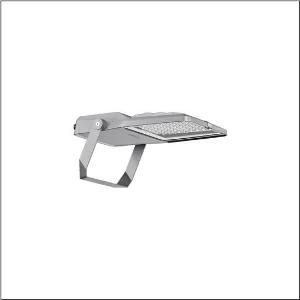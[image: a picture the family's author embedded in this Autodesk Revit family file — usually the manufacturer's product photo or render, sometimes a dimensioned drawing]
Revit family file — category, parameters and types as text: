
# Revit family: floodlight_fl_21_iq_mini___pl61_5xa7772c4c1a_7179
name_source: partatom
category: Lighting Fixtures
units: mm (PartAtom-declared; Revit-internal decimal feet)

## family parameters
Cut with Voids When Loaded = No
Host = Face
Light Source = No
Part Type = Normal
Room Calculation Point = No
Round Connector Dimension = Use Diameter
Shared = No

## types (1)
- --- (1 x LED, 12490 lm, 87.2 W, 4000K)
    Apparent Load = 87 VA
    CIE Flux Codes = 33 65 98 100 100
    Color Rendering = 70
    Color Temperature = 4000K
    Default Elevation = 1800 mm
    Description = Floodlight FL 21 iQ mini, floodlight, primary light control with lens, of PMMA, primary optical cover: protective disc, of toughened safety glass, transparent, light distribution: PL61, light emission: direct distribution, installation type: surface-mounted, LED, High Power LED, rated luminous flux: 12.490lm, luminous efficacy: 143lm/W, light colour: 740, colour temperature: 4000K, control: Street-Remote, Auto-Match, Temp-Guard, Night-Set, Smart-Wire, Desk-Remote (wireless, voltage-free reading and setting of iQ features in the workshop via application-optimized NFC function/RFID function), optimised constant luminous flux control (CLO 2.0), with terminal, 6-pole, mains connection: 220..240V, AC, 50/60Hz, start of lifetime: 87W, end of service life: 92W, reduction: 40W, luminaire housing, of diecast aluminium, powder-coated, Siteco® metallic grey (DB 702S), corrosivity category C5 mid according to DIN EN ISO 12944, sealing non-destructively replaceable, mounting bracket, of steel, galvanised, powder-coated, Siteco® metallic grey (DB 702S), protection rating (complete): IP66, insulation class (complete): insulation class II (safety insulation), certification: CE, ENEC, VDE, protection symbol: D, impact resistance: IK08, permissible operating ambient temperature: -40..+40°C, permissible operating ambient temperature for outdoor applications: -40..+50°C, standard: DIN EN 12944, LABS conformity tested according to VDMA 24364:2018-05, packaging unit: 1 piece

Light Distribution: PL61
    Height = 70 mm
    Lamp = 1 x LED
    Lamp Light Flux = 12490 lm
    Lamp Power = 87.2 W
    Lamp count = 1
    Length = 485 mm
    Luminous efficacy = 143 lm/W
    Manufacturer = Siteco
    ModVariant = No
    Model = 5XA7772C4C1A
    Number of Poles = 1
    OnlyDefault = Yes
    Power Factor = 1
    Product Name = Floodlight FL 21 iQ mini | PL61
    Product group = floodlight | pylon annexe
    ProductGroupID = 6200
    Protection Class = Protection class II
    Protection Degree = IP 66
    RLX_Detail_Level = 1
    RLX_Emergency_Light_Flux = 0 lm
    RLX_Emergency_Type = 0
    RLX_Emergency_Type_DB = No
    RlxData = <blob elided: 96213 chars, md5=36bcd006>
    Socket = socket
    Standby Power = 0 W
    System Light Flux = 12490 lm
    System Power = 87 W
    Type Comments = factory setting: luminous flux: 100 % | dim-lin: 254 | 456 mA
    Type Image = l_1006845.jpg
    URL = http://relux.com
    VarID = @adj_106047
    Voltage = 0 V
    Weight = 0.00 kg
    Width = 337 mm

## geometry (parser evidence)
native form markers: Blend x4, Sweep x13
no freeform markers — native parametric forms only
